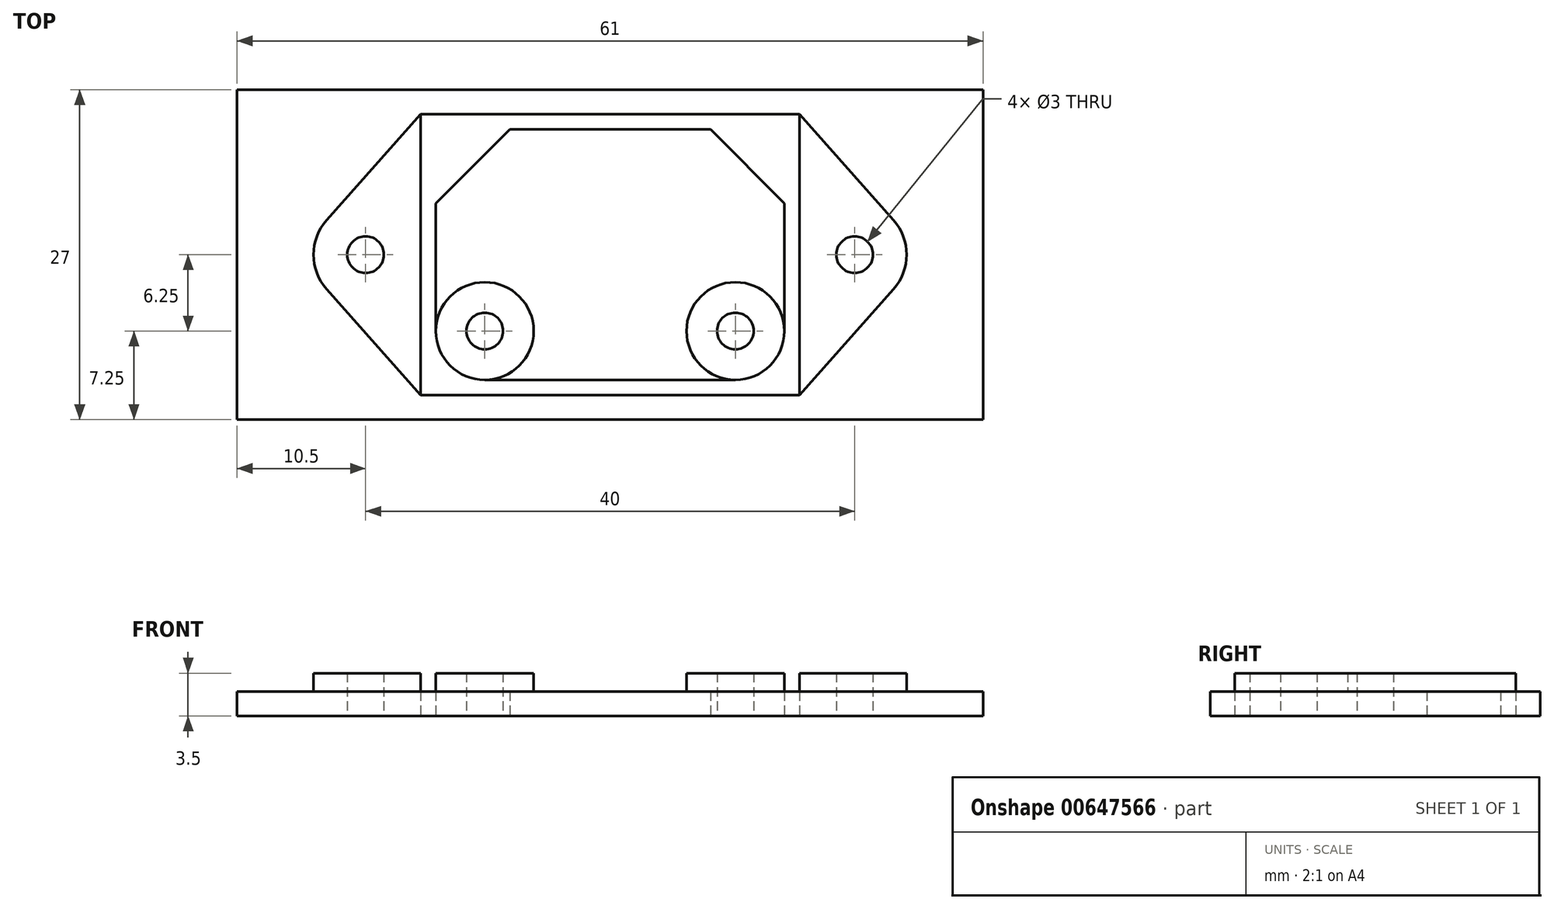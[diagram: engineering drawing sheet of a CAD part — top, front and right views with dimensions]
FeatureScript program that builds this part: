
annotation { "Feature Type Name" : "Feature", "Feature Type Description" : "" }
export const myFeature = defineFeature(function(context is Context, id is Id, definition is map)
    precondition{}
    {
        {
            var Q0;
            Q0=qCreatedBy(makeId("Top.planeOp"),FACE);
            var sketch = newSketch(context, id + "F0", { "sketchPlane" : qUnion([Q0])});
            skLineSegment(sketch, "E0.bottom", {"start": v(10.25, -9.75) * mm, "end": v(-10.25, -9.75) * mm});
            skLineSegment(sketch, "E0.top", {"start": v(8, 9.75) * mm, "end": v(-8, 9.75) * mm});
            skLineSegment(sketch, "E0.left", {"start": v(13.75, -6.25) * mm, "end": v(13.75, 4) * mm});
            skLineSegment(sketch, "E0.right", {"start": v(-13.75, -6.25) * mm, "end": v(-13.75, 4) * mm});
            skPoint(sketch, "E0.middle", {"position": v(0, 0) * mm});
            skLineSegment(sketch, "E1.bottom", {"start": v(15.5, -11.5) * mm, "end": v(-15.5, -11.5) * mm});
            skLineSegment(sketch, "E1.top", {"start": v(15.5, 11.5) * mm, "end": v(-15.5, 11.5) * mm});
            skLineSegment(sketch, "E2.bottom", {"start": v(-15.5, 11.5) * mm, "end": v(15.5, 11.5) * mm});
            skLineSegment(sketch, "E2.top", {"start": v(-15.5, -11.5) * mm, "end": v(15.5, -11.5) * mm});
            skLineSegment(sketch, "E2.left", {"start": v(-15.5, 11.5) * mm, "end": v(-15.5, -11.5) * mm});
            skLineSegment(sketch, "E2.right", {"start": v(15.5, 11.5) * mm, "end": v(15.5, -11.5) * mm});
            skLineSegment(sketch, "E3", {"start": v(-23.18, 2.82) * mm, "end": v(-15.5, 11.5) * mm});
            skLineSegment(sketch, "E4", {"start": v(-23.18, -2.82) * mm, "end": v(-15.5, -11.5) * mm});
            skLineSegment(sketch, "E5", {"start": v(23.18, 2.82) * mm, "end": v(15.5, 11.5) * mm});
            skLineSegment(sketch, "E6", {"start": v(23.18, -2.82) * mm, "end": v(15.5, -11.5) * mm});
            skLineSegment(sketch, "E7", {"start": v(-20, 0) * mm, "end": v(20, 0) * mm, "construction": true});
            skArc(sketch, "E8", {"start": v(-23.18, 2.82) * mm, "mid": v(-24.25, 0) * mm, "end": v(-23.18, -2.82) * mm});
            skArc(sketch, "E9", {"start": v(23.18, -2.82) * mm, "mid": v(24.25, 0) * mm, "end": v(23.18, 2.82) * mm});
            skCircle(sketch, "E10", {"center": v(-20, 0) * mm, "radius": 1.5 * mm});
            skCircle(sketch, "E11", {"center": v(20, 0) * mm, "radius": 1.5 * mm});
            skPoint(sketch, "E12.visualSharp", {"position": v(-13.75, -9.75) * mm});
            skArc(sketch, "E12.filletArc", {"start": v(-13.75, -6.25) * mm, "mid": v(-12.72, -8.72) * mm, "end": v(-10.25, -9.75) * mm});
            skPoint(sketch, "E13.visualSharp", {"position": v(13.75, -9.75) * mm});
            skArc(sketch, "E13.filletArc", {"start": v(10.25, -9.75) * mm, "mid": v(12.72, -8.72) * mm, "end": v(13.75, -6.25) * mm});
            skLineSegment(sketch, "E14", {"start": v(-13.75, 4) * mm, "end": v(-8, 9.75) * mm});
            skLineSegment(sketch, "E15", {"start": v(8, 9.75) * mm, "end": v(13.75, 4) * mm});
            skPoint(sketch, "E16.orphan", {"position": v(-13.75, 9.75) * mm});
            skPoint(sketch, "E17.orphan", {"position": v(13.75, 9.75) * mm});
            skLineSegment(sketch, "E18", {"start": v(30.5, 13.5) * mm, "end": v(30.5, -13.5) * mm});
            skLineSegment(sketch, "E19", {"start": v(-30.5, 13.5) * mm, "end": v(-30.5, -13.5) * mm});
            skPoint(sketch, "E20", {"position": v(-30.5, 0) * mm});
            skLineSegment(sketch, "E21", {"start": v(-30.5, 13.5) * mm, "end": v(30.5, 13.5) * mm});
            skLineSegment(sketch, "E22", {"start": v(-30.5, -13.5) * mm, "end": v(30.5, -13.5) * mm});
            skCircle(sketch, "E23", {"center": v(-10.25, -6.25) * mm, "radius": 1.5 * mm});
            skCircle(sketch, "E24", {"center": v(10.25, -6.25) * mm, "radius": 1.5 * mm});
            skCircle(sketch, "E25", {"center": v(-10.25, -6.25) * mm, "radius": 4 * mm});
            skCircle(sketch, "E26", {"center": v(10.25, -6.25) * mm, "radius": 4 * mm});
            skLineSegment(sketch, "E27.0", {"start": v(8.2, 10.25) * mm, "end": v(14.25, 4.2) * mm});
            skLineSegment(sketch, "E27.1", {"start": v(14.25, -6.25) * mm, "end": v(14.25, 4.2) * mm});
            skLineSegment(sketch, "E27.2", {"start": v(8.2, 10.25) * mm, "end": v(-8.2, 10.25) * mm});
            skArc(sketch, "E27.3", {"start": v(10.25, -10.25) * mm, "mid": v(13.08, -9.08) * mm, "end": v(14.25, -6.25) * mm});
            skLineSegment(sketch, "E27.4", {"start": v(-14.25, 4.2) * mm, "end": v(-8.2, 10.25) * mm});
            skLineSegment(sketch, "E27.5", {"start": v(-14.25, -6.25) * mm, "end": v(-14.25, 4.2) * mm});
            skArc(sketch, "E27.6", {"start": v(-14.25, -6.25) * mm, "mid": v(-13.08, -9.08) * mm, "end": v(-10.25, -10.25) * mm});
            skLineSegment(sketch, "E27.7", {"start": v(10.25, -10.25) * mm, "end": v(-10.25, -10.25) * mm});
            skSolve(sketch);
        }
        {
            var Q0;
            Q0 = qSketchRegion(id + "F0", true);
            var Q1;
            Q1=makeQuery(id+"F0.imprint","IMPRINT",FACE,{"disambiguationData":[TD([[makeQuery(id+"F0.imprint","IMPRINT",EDGE,{"derivedFrom":sQuery(id+"F0.wireOp",EDGE,"E2.left")}),-1.0]])]});
            var Q2;
            Q2=makeQuery(id+"F0.imprint","IMPRINT",FACE,{"disambiguationData":[TD([[makeQuery(id+"F0.imprint","IMPRINT",EDGE,{"derivedFrom":sQuery(id+"F0.wireOp",EDGE,"E0.bottom")}),-1.0]])]});
            var Q3;
            Q3=makeQuery(id+"F0.imprint","IMPRINT",FACE,{"disambiguationData":[TD([[makeQuery(id+"F0.imprint","IMPRINT",EDGE,{"derivedFrom":sQuery(id+"F0.wireOp",EDGE,"E2.bottom")}),-1.0]])]});
            var Q4;
            Q4=makeQuery(id+"F0.imprint","IMPRINT",FACE,{"disambiguationData":[TD([[makeQuery(id+"F0.imprint","IMPRINT",EDGE,{"derivedFrom":sQuery(id+"F0.wireOp",EDGE,"E0.bottom")}),1.0]])]});
            var Q5;
            Q5=makeQuery(id+"F0.imprint","IMPRINT",FACE,{"disambiguationData":[TD([[makeQuery(id+"F0.imprint","IMPRINT",EDGE,{"derivedFrom":sQuery(id+"F0.wireOp",EDGE,"E2.right")}),1.0]])]});
            var Q6;
            Q6=makeQuery(id+"F0.imprint","IMPRINT",FACE,{"disambiguationData":[TD([[makeQuery(id+"F0.imprint","IMPRINT",EDGE,{"derivedFrom":sQuery(id+"F0.wireOp",EDGE,"E0.top")}),1.0]])]});
            var Q7;
            Q7=makeQuery(id+"F0.imprint","IMPRINT",FACE,{"disambiguationData":[TD([[makeQuery(id+"F0.imprint","IMPRINT",EDGE,{"derivedFrom":sQuery(id+"F0.wireOp",EDGE,"E0.top")}),-1.0]])]});
            var Q8;
            {var subQ4=sQuery(id+"F0.wireOp",EDGE,"E12.filletArc");Q8=makeQuery(id+"F0.imprint","IMPRINT",FACE,{"disambiguationData":[TD([[makeQuery(id+"F0.imprint","IMPRINT",EDGE,{"derivedFrom":subQ4}),-1.0]])]});}
            var Q9;
            {var subQ0=sQuery(id+"F0.wireOp",EDGE,"E13.filletArc");Q9=makeQuery(id+"F0.imprint","IMPRINT",FACE,{"disambiguationData":[TD([[makeQuery(id+"F0.imprint","IMPRINT",EDGE,{"derivedFrom":subQ0}),-1.0]])]});}
            extrude(context, id + "F1", {"entities" : qUnion([Q0, Q1, Q2, Q3, Q4, Q5, Q6, Q7, Q8, Q9]), "depth" : 2 * mm, "offsetDistance" : 25 * mm});
        }
        {
            var Q0;
            Q0=makeQuery(id+"F0.imprint","IMPRINT",FACE,{"disambiguationData":[TD([[makeQuery(id+"F0.imprint","IMPRINT",EDGE,{"derivedFrom":sQuery(id+"F0.wireOp",EDGE,"E2.left")}),-1.0]])]});
            var Q1;
            Q1=makeQuery(id+"F0.imprint","IMPRINT",FACE,{"disambiguationData":[TD([[makeQuery(id+"F0.imprint","IMPRINT",EDGE,{"derivedFrom":sQuery(id+"F0.wireOp",EDGE,"E2.bottom")}),-1.0]])]});
            var Q2;
            Q2=makeQuery(id+"F0.imprint","IMPRINT",FACE,{"disambiguationData":[TD([[makeQuery(id+"F0.imprint","IMPRINT",EDGE,{"derivedFrom":sQuery(id+"F0.wireOp",EDGE,"E2.right")}),1.0]])]});
            var Q3;
            {var subQ0=sQuery(id+"F0.wireOp",EDGE,"E12.filletArc");Q3=makeQuery(id+"F0.imprint","IMPRINT",FACE,{"disambiguationData":[TD([[makeQuery(id+"F0.imprint","IMPRINT",EDGE,{"derivedFrom":subQ0}),1.0]])]});}
            var Q4;
            {var subQ4=sQuery(id+"F0.wireOp",EDGE,"E12.filletArc");Q4=makeQuery(id+"F0.imprint","IMPRINT",FACE,{"disambiguationData":[TD([[makeQuery(id+"F0.imprint","IMPRINT",EDGE,{"derivedFrom":subQ4}),-1.0]])]});}
            var Q5;
            {var subQ0=sQuery(id+"F0.wireOp",EDGE,"E13.filletArc");Q5=makeQuery(id+"F0.imprint","IMPRINT",FACE,{"disambiguationData":[TD([[makeQuery(id+"F0.imprint","IMPRINT",EDGE,{"derivedFrom":subQ0}),1.0]])]});}
            var Q6;
            {var subQ0=sQuery(id+"F0.wireOp",EDGE,"E13.filletArc");Q6=makeQuery(id+"F0.imprint","IMPRINT",FACE,{"disambiguationData":[TD([[makeQuery(id+"F0.imprint","IMPRINT",EDGE,{"derivedFrom":subQ0}),-1.0]])]});}
            extrude(context, id + "F2", {"entities" : qUnion([Q0, Q1, Q2, Q3, Q4, Q5, Q6]), "operationType" : NewBodyOperationType.ADD, "depth" : 3.5 * mm, "offsetDistance" : 25 * mm});
        }
    });
